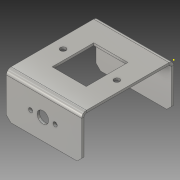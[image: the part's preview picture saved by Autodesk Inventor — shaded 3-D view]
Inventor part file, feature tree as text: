
AUTODESK INVENTOR PART (.ipt)
format: ipt  version: 2016 SP1 (Build 200210100, 210)  size: 162,304 bytes
history: native  units: in
note: dims shown in document units (in); Inventor stores cm internally (conversion verified against a paired STEP export)
features: sketch x7, sheet_metal_op x4, hole x4, other x4
ambient origin geometry x8: Origin, YZ Plane, XZ Plane, XY Plane, X Axis, Y Axis, Z Axis, Center Point
bodies: Solid1 (feature_tree)
feature tree (19):
  sheet_metal_op  "Face1"
  sheet_metal_op  "Flange1"
  hole  "Hole1"  [1 undecoded]
  sketch  "Sketch5"  dims[d10=0.2564in]
  hole  "Hole2"  [1 undecoded]
  hole  "Hole3"  [1 undecoded]
  sketch  "Sketch6"  dims[d11=0.0641in]
  hole  "Hole4"  [1 undecoded]
  other  "Corner Chamfer1"
  sketch  "Sketch1"  dims[d0=2.06in d1=2.515in]
  other  "Plate1"
  sketch  "Sketch2"  dims[d2=0.0641in d3=0.0641in]
  other  "Plate2"
  sheet_metal_op  "Bend1"
  sheet_metal_op  "Corner1"
  sketch  "Sketch3"  dims[d4=0.0321in d5=0.1282in]
  sketch  "Sketch4"  dims[d6=0.0641in d7=1.2in d8=90.0deg d9=0.0641in]
  sketch  "Sketch7"  dims[d12=0.0641in d13=0.688in d14=1.827in d15=0.563in d16=1.497in d17=0.0641in d18=0.0in d19=0.295in d20=1.765in d21=0.153in d22=0.75in d23=0.375in d24=0.25in d25=0.5635in d26=0.0641in d27=0.8108in d28=0.631in d29=0.665in d30=1.0in d31=1.335in d32=0.116in d33=0.75in d34=0.375in d35=0.25in d36=0.5635in d37=0.0641in d38=0.8108in d39=0.315in d40=0.75in d41=0.375in d42=0.25in d43=0.5635in d44=0.0641in d45=0.8108in d46=0.17in d47=0.75in d48=0.375in d49=0.25in d50=0.5635in d51=0.0641in d52=0.8108in d53=0.125in d54=0.25in d55=45.0deg]
  other  "Cut1"
note: 4 required parameter values undecoded (feature->parameter linkage not recoverable at this tier; creation-order binding heuristic only, values carry confidence <= 0.55)
